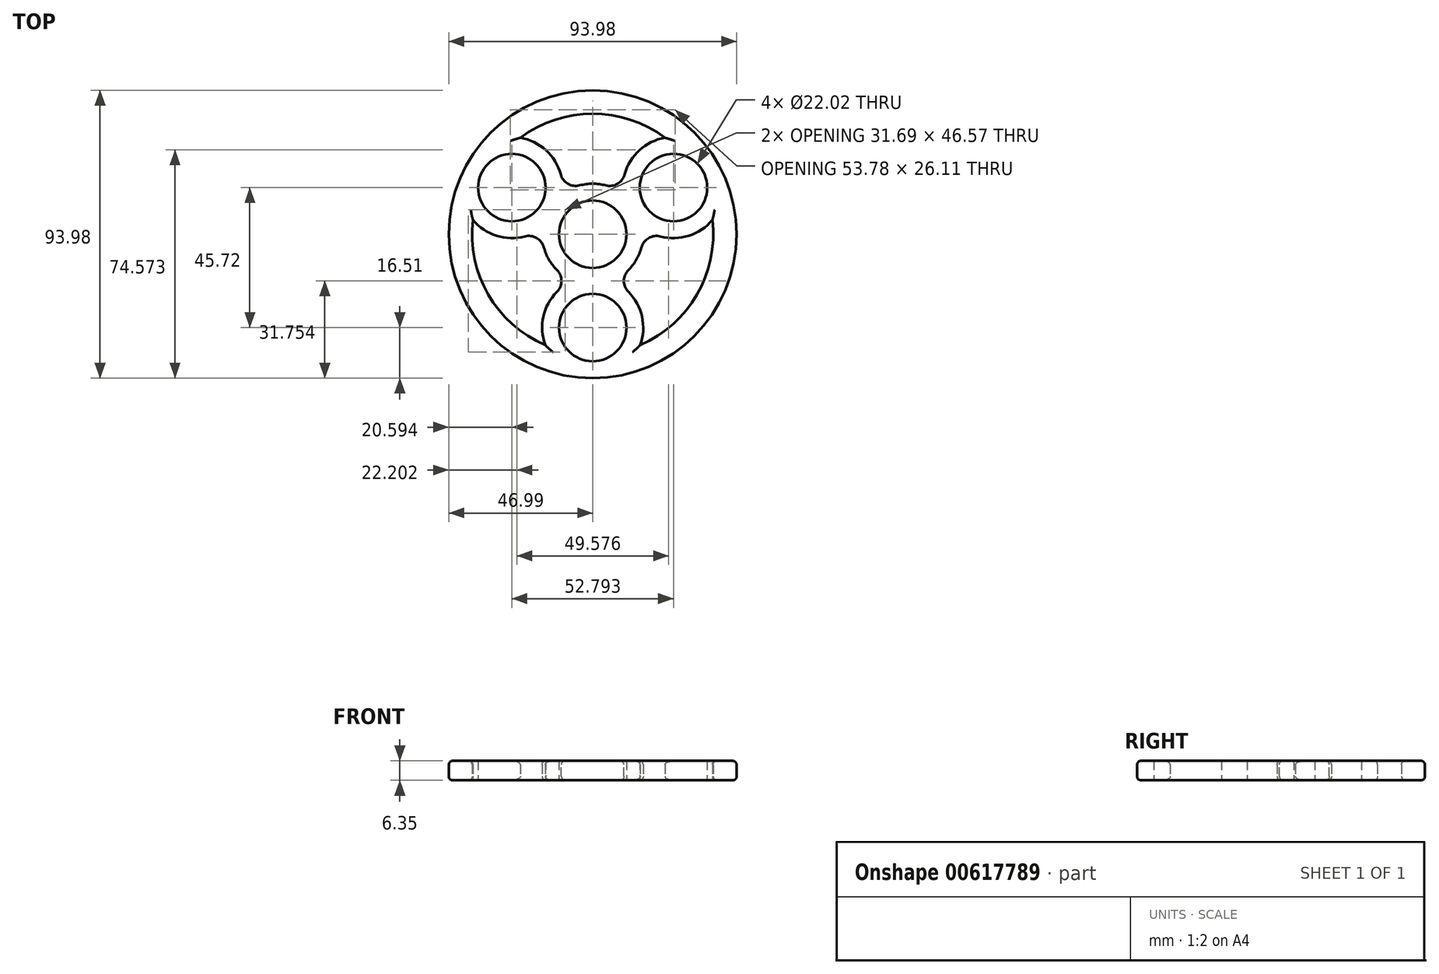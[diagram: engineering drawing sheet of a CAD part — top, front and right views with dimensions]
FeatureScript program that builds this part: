
annotation { "Feature Type Name" : "Feature", "Feature Type Description" : "" }
export const myFeature = defineFeature(function(context is Context, id is Id, definition is map)
    precondition{}
    {
        {
            var Q0;
            Q0=qCreatedBy(makeId("Top.planeOp"),FACE);
            var sketch = newSketch(context, id + "F0", { "sketchPlane" : qUnion([Q0])});
            skCircle(sketch, "E0", {"center": v(0, 0) * mm, "radius": 11.01 * mm});
            skLineSegment(sketch, "E1", {"start": v(0, 0) * mm, "end": v(-26.4, 15.24) * mm});
            skLineSegment(sketch, "E2", {"start": v(0, 0) * mm, "end": v(0, -30.48) * mm});
            skLineSegment(sketch, "E3", {"start": v(0, 0) * mm, "end": v(26.4, 15.24) * mm});
            skCircle(sketch, "E4", {"center": v(-26.4, 15.24) * mm, "radius": 11.01 * mm});
            skCircle(sketch, "E5", {"center": v(26.4, 15.24) * mm, "radius": 11.01 * mm});
            skCircle(sketch, "E6", {"center": v(0, -30.48) * mm, "radius": 11.01 * mm});
            skCircle(sketch, "E7", {"center": v(-26.4, 15.24) * mm, "radius": 16.51 * mm});
            skCircle(sketch, "E8", {"center": v(0, 0) * mm, "radius": 16.51 * mm});
            skCircle(sketch, "E9", {"center": v(0, -30.48) * mm, "radius": 16.51 * mm});
            skCircle(sketch, "E10", {"center": v(26.4, 15.24) * mm, "radius": 16.51 * mm});
            skCircle(sketch, "E11", {"center": v(0, 0) * mm, "radius": 47 * mm});
            skCircle(sketch, "E12", {"center": v(0, 0) * mm, "radius": 39.37 * mm});
            skSolve(sketch);
        }
        {
            var Q0;
            Q0 = qSketchRegion(id + "F0", true);
            var Q1;
            Q1=makeQuery(id+"F0.imprint","IMPRINT",FACE,{"disambiguationData":[TD([[makeQuery(id+"F0.imprint","IMPRINT",EDGE,{"derivedFrom":sQuery(id+"F0.wireOp",EDGE,"E4")}),-1.0]])]});
            var Q2;
            {var subQ1=sQuery(id+"F0.wireOp",EDGE,"E1");var subQ5=sQuery(id+"F0.wireOp",EDGE,"E0");var subQ6=makeQuery(id+"F0.imprint","INTERSECT",VERTEX,{"derivedFrom":[subQ5,subQ1]});Q2=makeQuery(id+"F0.imprint","IMPRINT",FACE,{"disambiguationData":[TD([[makeQuery(id+"F0.imprint","IMPRINT",EDGE,{"disambiguationData":[TD([[subQ6,1.0]])],"derivedFrom":subQ5}),-1.0]])]});}
            var Q3;
            {var subQ0=sQuery(id+"F0.wireOp",EDGE,"E8");var subQ1=sQuery(id+"F0.wireOp",EDGE,"E3");var subQ2=makeQuery(id+"F0.imprint","INTERSECT",VERTEX,{"derivedFrom":[subQ1,subQ0]});Q3=makeQuery(id+"F0.imprint","IMPRINT",FACE,{"disambiguationData":[TD([[makeQuery(id+"F0.imprint","IMPRINT",EDGE,{"disambiguationData":[TD([[subQ2,1.0]])],"derivedFrom":subQ1}),1.0]])]});}
            var Q4;
            {var subQ0=sQuery(id+"F0.wireOp",EDGE,"E8");var subQ1=sQuery(id+"F0.wireOp",EDGE,"E3");var subQ2=makeQuery(id+"F0.imprint","INTERSECT",VERTEX,{"derivedFrom":[subQ1,subQ0]});Q4=makeQuery(id+"F0.imprint","IMPRINT",FACE,{"disambiguationData":[TD([[makeQuery(id+"F0.imprint","IMPRINT",EDGE,{"disambiguationData":[TD([[subQ2,1.0]])],"derivedFrom":subQ1}),-1.0]])]});}
            var Q5;
            Q5=makeQuery(id+"F0.imprint","IMPRINT",FACE,{"disambiguationData":[TD([[makeQuery(id+"F0.imprint","IMPRINT",EDGE,{"derivedFrom":sQuery(id+"F0.wireOp",EDGE,"E5")}),-1.0]])]});
            var Q6;
            {var subQ5=sQuery(id+"F0.wireOp",EDGE,"E3");var subQ6=sQuery(id+"F0.wireOp",EDGE,"E0");var subQ7=makeQuery(id+"F0.imprint","INTERSECT",VERTEX,{"derivedFrom":[subQ6,subQ5]});Q6=makeQuery(id+"F0.imprint","IMPRINT",FACE,{"disambiguationData":[TD([[makeQuery(id+"F0.imprint","IMPRINT",EDGE,{"disambiguationData":[TD([[subQ7,1.0]])],"derivedFrom":subQ6}),-1.0]])]});}
            var Q7;
            {var subQ0=sQuery(id+"F0.wireOp",EDGE,"E8");var subQ1=sQuery(id+"F0.wireOp",EDGE,"E2");var subQ2=makeQuery(id+"F0.imprint","INTERSECT",VERTEX,{"derivedFrom":[subQ1,subQ0]});Q7=makeQuery(id+"F0.imprint","IMPRINT",FACE,{"disambiguationData":[TD([[makeQuery(id+"F0.imprint","IMPRINT",EDGE,{"disambiguationData":[TD([[subQ2,1.0]])],"derivedFrom":subQ1}),1.0]])]});}
            var Q8;
            {var subQ0=sQuery(id+"F0.wireOp",EDGE,"E8");var subQ1=sQuery(id+"F0.wireOp",EDGE,"E2");var subQ2=makeQuery(id+"F0.imprint","INTERSECT",VERTEX,{"derivedFrom":[subQ1,subQ0]});Q8=makeQuery(id+"F0.imprint","IMPRINT",FACE,{"disambiguationData":[TD([[makeQuery(id+"F0.imprint","IMPRINT",EDGE,{"disambiguationData":[TD([[subQ2,1.0]])],"derivedFrom":subQ1}),-1.0]])]});}
            var Q9;
            {var subQ1=sQuery(id+"F0.wireOp",EDGE,"E1");var subQ5=sQuery(id+"F0.wireOp",EDGE,"E0");var subQ6=makeQuery(id+"F0.imprint","INTERSECT",VERTEX,{"derivedFrom":[subQ5,subQ1]});Q9=makeQuery(id+"F0.imprint","IMPRINT",FACE,{"disambiguationData":[TD([[makeQuery(id+"F0.imprint","IMPRINT",EDGE,{"disambiguationData":[TD([[subQ6,-1.0]])],"derivedFrom":subQ5}),-1.0]])]});}
            var Q10;
            {var subQ0=sQuery(id+"F0.wireOp",EDGE,"E8");var subQ1=sQuery(id+"F0.wireOp",EDGE,"E1");var subQ2=makeQuery(id+"F0.imprint","INTERSECT",VERTEX,{"derivedFrom":[subQ1,subQ0]});Q10=makeQuery(id+"F0.imprint","IMPRINT",FACE,{"disambiguationData":[TD([[makeQuery(id+"F0.imprint","IMPRINT",EDGE,{"disambiguationData":[TD([[subQ2,1.0]])],"derivedFrom":subQ1}),-1.0]])]});}
            var Q11;
            {var subQ0=sQuery(id+"F0.wireOp",EDGE,"E8");var subQ1=sQuery(id+"F0.wireOp",EDGE,"E1");var subQ2=makeQuery(id+"F0.imprint","INTERSECT",VERTEX,{"derivedFrom":[subQ1,subQ0]});Q11=makeQuery(id+"F0.imprint","IMPRINT",FACE,{"disambiguationData":[TD([[makeQuery(id+"F0.imprint","IMPRINT",EDGE,{"disambiguationData":[TD([[subQ2,1.0]])],"derivedFrom":subQ1}),1.0]])]});}
            var Q12;
            Q12=makeQuery(id+"F0.imprint","IMPRINT",FACE,{"disambiguationData":[TD([[makeQuery(id+"F0.imprint","IMPRINT",EDGE,{"derivedFrom":sQuery(id+"F0.wireOp",EDGE,"E6")}),-1.0]])]});
            extrude(context, id + "F1", {"entities" : qUnion([Q0, Q1, Q2, Q3, Q4, Q5, Q6, Q7, Q8, Q9, Q10, Q11, Q12]), "depth" : 6.35 * mm, "offsetDistance" : 25.4 * mm});
        }
        {
            var Q0;
            {var subQ0=sQuery(id+"F0.wireOp",EDGE,"E10");var subQ1=sQuery(id+"F0.wireOp",EDGE,"E8");Q0=makeQuery(id+"F1.opExtrude","SWEPT_EDGE",EDGE,{"disambiguationData":[OSD([subQ1,subQ0]),TDD([makeQuery(id+"F0.imprint","INTERSECT",VERTEX,{"disambiguationData":[OD(1.0)],"derivedFrom":[subQ1,subQ0]})])]});}
            var Q1;
            {var subQ0=sQuery(id+"F0.wireOp",EDGE,"E10");var subQ1=sQuery(id+"F0.wireOp",EDGE,"E8");Q1=makeQuery(id+"F1.opExtrude","SWEPT_EDGE",EDGE,{"disambiguationData":[OSD([subQ1,subQ0]),TDD([makeQuery(id+"F0.imprint","INTERSECT",VERTEX,{"disambiguationData":[OD(0.0)],"derivedFrom":[subQ1,subQ0]})])]});}
            var Q2;
            {var subQ0=sQuery(id+"F0.wireOp",EDGE,"E9");var subQ1=sQuery(id+"F0.wireOp",EDGE,"E8");Q2=makeQuery(id+"F1.opExtrude","SWEPT_EDGE",EDGE,{"disambiguationData":[OSD([subQ1,subQ0]),TDD([makeQuery(id+"F0.imprint","INTERSECT",VERTEX,{"disambiguationData":[OD(1.0)],"derivedFrom":[subQ1,subQ0]})])]});}
            var Q3;
            {var subQ0=sQuery(id+"F0.wireOp",EDGE,"E9");var subQ1=sQuery(id+"F0.wireOp",EDGE,"E8");Q3=makeQuery(id+"F1.opExtrude","SWEPT_EDGE",EDGE,{"disambiguationData":[OSD([subQ1,subQ0]),TDD([makeQuery(id+"F0.imprint","INTERSECT",VERTEX,{"disambiguationData":[OD(0.0)],"derivedFrom":[subQ1,subQ0]})])]});}
            var Q4;
            {var subQ0=sQuery(id+"F0.wireOp",EDGE,"E8");var subQ1=sQuery(id+"F0.wireOp",EDGE,"E7");Q4=makeQuery(id+"F1.opExtrude","SWEPT_EDGE",EDGE,{"disambiguationData":[OSD([subQ1,subQ0]),TDD([makeQuery(id+"F0.imprint","INTERSECT",VERTEX,{"disambiguationData":[OD(0.0)],"derivedFrom":[subQ1,subQ0]})])]});}
            var Q5;
            {var subQ0=sQuery(id+"F0.wireOp",EDGE,"E8");var subQ1=sQuery(id+"F0.wireOp",EDGE,"E7");Q5=makeQuery(id+"F1.opExtrude","SWEPT_EDGE",EDGE,{"disambiguationData":[OSD([subQ1,subQ0]),TDD([makeQuery(id+"F0.imprint","INTERSECT",VERTEX,{"disambiguationData":[OD(1.0)],"derivedFrom":[subQ1,subQ0]})])]});}
            fillet(context, id + "F2", {"entities" : qUnion([Q0, Q1, Q2, Q3, Q4, Q5]), "radius" : 5.08 * mm, "tangentPropagation" : true, "allowEdgeOverflow" : false});
        }
        {
            var Q0;
            {var subQ0=sQuery(id+"F0.wireOp",EDGE,"E12");Q0=makeQuery(id+"F1.opExtrude","CAP_EDGE",EDGE,{"disambiguationData":[OSD([subQ0]),TDD([makeQuery(id+"F0.imprint","IMPRINT",EDGE,{"disambiguationData":[TD([[makeQuery(id+"F0.imprint","INTERSECT",VERTEX,{"disambiguationData":[OD(0.0)],"derivedFrom":[sQuery(id+"F0.wireOp",EDGE,"E7"),subQ0]}),1.0]])],"derivedFrom":subQ0})])],"isStart":false});}
            var Q1;
            {var subQ0=sQuery(id+"F0.wireOp",EDGE,"E10");Q1=makeQuery(id+"F1.opExtrude","CAP_EDGE",EDGE,{"disambiguationData":[OSD([subQ0]),TDD([makeQuery(id+"F0.imprint","IMPRINT",EDGE,{"disambiguationData":[TD([[makeQuery(id+"F0.imprint","INTERSECT",VERTEX,{"disambiguationData":[OD(1.0)],"derivedFrom":[sQuery(id+"F0.wireOp",EDGE,"E8"),subQ0]}),1.0]])],"derivedFrom":subQ0})])],"isStart":false});}
            var Q2;
            {var subQ0=sQuery(id+"F0.wireOp",EDGE,"E8");Q2=makeQuery(id+"F1.opExtrude","CAP_EDGE",EDGE,{"disambiguationData":[OSD([subQ0]),TDD([makeQuery(id+"F0.imprint","IMPRINT",EDGE,{"disambiguationData":[TD([[makeQuery(id+"F0.imprint","INTERSECT",VERTEX,{"disambiguationData":[OD(1.0)],"derivedFrom":[sQuery(id+"F0.wireOp",EDGE,"E7"),subQ0]}),1.0]])],"derivedFrom":subQ0})])],"isStart":false});}
            var Q3;
            {var subQ0=sQuery(id+"F0.wireOp",EDGE,"E7");Q3=makeQuery(id+"F1.opExtrude","CAP_EDGE",EDGE,{"disambiguationData":[OSD([subQ0]),TDD([makeQuery(id+"F0.imprint","IMPRINT",EDGE,{"disambiguationData":[TD([[makeQuery(id+"F0.imprint","INTERSECT",VERTEX,{"disambiguationData":[OD(0.0)],"derivedFrom":[subQ0,sQuery(id+"F0.wireOp",EDGE,"E12")]}),1.0]])],"derivedFrom":subQ0})])],"isStart":false});}
            var Q4;
            {var subQ0=sQuery(id+"F0.wireOp",EDGE,"E8");Q4=makeQuery(id+"F1.opExtrude","CAP_EDGE",EDGE,{"disambiguationData":[OSD([subQ0]),TDD([makeQuery(id+"F0.imprint","IMPRINT",EDGE,{"disambiguationData":[TD([[makeQuery(id+"F0.imprint","INTERSECT",VERTEX,{"disambiguationData":[OD(0.0)],"derivedFrom":[subQ0,sQuery(id+"F0.wireOp",EDGE,"E10")]}),1.0]])],"derivedFrom":subQ0})])],"isStart":false});}
            var Q5;
            {var subQ0=sQuery(id+"F0.wireOp",EDGE,"E10");Q5=makeQuery(id+"F1.opExtrude","CAP_EDGE",EDGE,{"disambiguationData":[OSD([subQ0]),TDD([makeQuery(id+"F0.imprint","IMPRINT",EDGE,{"disambiguationData":[TD([[makeQuery(id+"F0.imprint","INTERSECT",VERTEX,{"disambiguationData":[OD(0.0)],"derivedFrom":[sQuery(id+"F0.wireOp",EDGE,"E8"),subQ0]}),-1.0]])],"derivedFrom":subQ0})])],"isStart":false});}
            var Q6;
            {var subQ0=sQuery(id+"F0.wireOp",EDGE,"E9");Q6=makeQuery(id+"F1.opExtrude","CAP_EDGE",EDGE,{"disambiguationData":[OSD([subQ0]),TDD([makeQuery(id+"F0.imprint","IMPRINT",EDGE,{"disambiguationData":[TD([[makeQuery(id+"F0.imprint","INTERSECT",VERTEX,{"disambiguationData":[OD(1.0)],"derivedFrom":[sQuery(id+"F0.wireOp",EDGE,"E8"),subQ0]}),1.0]])],"derivedFrom":subQ0})])],"isStart":false});}
            var Q7;
            {var subQ0=sQuery(id+"F0.wireOp",EDGE,"E12");Q7=makeQuery(id+"F1.opExtrude","CAP_EDGE",EDGE,{"disambiguationData":[OSD([subQ0]),TDD([makeQuery(id+"F0.imprint","IMPRINT",EDGE,{"disambiguationData":[TD([[makeQuery(id+"F0.imprint","INTERSECT",VERTEX,{"disambiguationData":[OD(1.0)],"derivedFrom":[sQuery(id+"F0.wireOp",EDGE,"E9"),subQ0]}),-1.0]])],"derivedFrom":subQ0})])],"isStart":false});}
            var Q8;
            Q8=makeQuery(id+"F1.opExtrude","CAP_EDGE",EDGE,{"disambiguationData":[OSD([sQuery(id+"F0.wireOp",EDGE,"E11")])],"isStart":false});
            var Q9;
            {var subQ0=sQuery(id+"F0.wireOp",EDGE,"E9");Q9=makeQuery(id+"F1.opExtrude","CAP_EDGE",EDGE,{"disambiguationData":[OSD([subQ0]),TDD([makeQuery(id+"F0.imprint","IMPRINT",EDGE,{"disambiguationData":[TD([[makeQuery(id+"F0.imprint","INTERSECT",VERTEX,{"disambiguationData":[OD(0.0)],"derivedFrom":[sQuery(id+"F0.wireOp",EDGE,"E8"),subQ0]}),-1.0]])],"derivedFrom":subQ0})])],"isStart":false});}
            var Q10;
            {var subQ0=sQuery(id+"F0.wireOp",EDGE,"E8");Q10=makeQuery(id+"F1.opExtrude","CAP_EDGE",EDGE,{"disambiguationData":[OSD([subQ0]),TDD([makeQuery(id+"F0.imprint","IMPRINT",EDGE,{"disambiguationData":[TD([[makeQuery(id+"F0.imprint","INTERSECT",VERTEX,{"disambiguationData":[OD(0.0)],"derivedFrom":[sQuery(id+"F0.wireOp",EDGE,"E7"),subQ0]}),-1.0]])],"derivedFrom":subQ0})])],"isStart":false});}
            var Q11;
            {var subQ0=sQuery(id+"F0.wireOp",EDGE,"E7");Q11=makeQuery(id+"F1.opExtrude","CAP_EDGE",EDGE,{"disambiguationData":[OSD([subQ0]),TDD([makeQuery(id+"F0.imprint","IMPRINT",EDGE,{"disambiguationData":[TD([[makeQuery(id+"F0.imprint","INTERSECT",VERTEX,{"disambiguationData":[OD(1.0)],"derivedFrom":[subQ0,sQuery(id+"F0.wireOp",EDGE,"E12")]}),-1.0]])],"derivedFrom":subQ0})])],"isStart":false});}
            var Q12;
            {var subQ0=sQuery(id+"F0.wireOp",EDGE,"E12");Q12=makeQuery(id+"F1.opExtrude","CAP_EDGE",EDGE,{"disambiguationData":[OSD([subQ0]),TDD([makeQuery(id+"F0.imprint","IMPRINT",EDGE,{"disambiguationData":[TD([[makeQuery(id+"F0.imprint","INTERSECT",VERTEX,{"disambiguationData":[OD(1.0)],"derivedFrom":[sQuery(id+"F0.wireOp",EDGE,"E7"),subQ0]}),-1.0]])],"derivedFrom":subQ0})])],"isStart":false});}
            fillet(context, id + "F3", {"entities" : qUnion([Q0, Q1, Q2, Q3, Q4, Q5, Q6, Q7, Q8, Q9, Q10, Q11, Q12]), "radius" : 1.27 * mm, "tangentPropagation" : true, "allowEdgeOverflow" : false});
        }
        {
            var Q0;
            Q0=makeQuery(id+"F1.opExtrude","CAP_EDGE",EDGE,{"disambiguationData":[OSD([sQuery(id+"F0.wireOp",EDGE,"E11")])],"isStart":true});
            var Q1;
            {var subQ0=sQuery(id+"F0.wireOp",EDGE,"E12");Q1=makeQuery(id+"F1.opExtrude","CAP_EDGE",EDGE,{"disambiguationData":[OSD([subQ0]),TDD([makeQuery(id+"F0.imprint","IMPRINT",EDGE,{"disambiguationData":[TD([[makeQuery(id+"F0.imprint","INTERSECT",VERTEX,{"disambiguationData":[OD(0.0)],"derivedFrom":[sQuery(id+"F0.wireOp",EDGE,"E7"),subQ0]}),1.0]])],"derivedFrom":subQ0})])],"isStart":true});}
            var Q2;
            {var subQ0=sQuery(id+"F0.wireOp",EDGE,"E10");Q2=makeQuery(id+"F1.opExtrude","CAP_EDGE",EDGE,{"disambiguationData":[OSD([subQ0]),TDD([makeQuery(id+"F0.imprint","IMPRINT",EDGE,{"disambiguationData":[TD([[makeQuery(id+"F0.imprint","INTERSECT",VERTEX,{"disambiguationData":[OD(1.0)],"derivedFrom":[sQuery(id+"F0.wireOp",EDGE,"E8"),subQ0]}),1.0]])],"derivedFrom":subQ0})])],"isStart":true});}
            var Q3;
            {var subQ0=sQuery(id+"F0.wireOp",EDGE,"E10");Q3=makeQuery(id+"F1.opExtrude","CAP_EDGE",EDGE,{"disambiguationData":[OSD([subQ0]),TDD([makeQuery(id+"F0.imprint","IMPRINT",EDGE,{"disambiguationData":[TD([[makeQuery(id+"F0.imprint","INTERSECT",VERTEX,{"disambiguationData":[OD(0.0)],"derivedFrom":[sQuery(id+"F0.wireOp",EDGE,"E8"),subQ0]}),-1.0]])],"derivedFrom":subQ0})])],"isStart":true});}
            var Q4;
            {var subQ0=sQuery(id+"F0.wireOp",EDGE,"E8");Q4=makeQuery(id+"F1.opExtrude","CAP_EDGE",EDGE,{"disambiguationData":[OSD([subQ0]),TDD([makeQuery(id+"F0.imprint","IMPRINT",EDGE,{"disambiguationData":[TD([[makeQuery(id+"F0.imprint","INTERSECT",VERTEX,{"disambiguationData":[OD(0.0)],"derivedFrom":[subQ0,sQuery(id+"F0.wireOp",EDGE,"E10")]}),1.0]])],"derivedFrom":subQ0})])],"isStart":true});}
            var Q5;
            {var subQ0=sQuery(id+"F0.wireOp",EDGE,"E8");Q5=makeQuery(id+"F1.opExtrude","CAP_EDGE",EDGE,{"disambiguationData":[OSD([subQ0]),TDD([makeQuery(id+"F0.imprint","IMPRINT",EDGE,{"disambiguationData":[TD([[makeQuery(id+"F0.imprint","INTERSECT",VERTEX,{"disambiguationData":[OD(1.0)],"derivedFrom":[sQuery(id+"F0.wireOp",EDGE,"E7"),subQ0]}),1.0]])],"derivedFrom":subQ0})])],"isStart":true});}
            var Q6;
            {var subQ0=sQuery(id+"F0.wireOp",EDGE,"E7");Q6=makeQuery(id+"F1.opExtrude","CAP_EDGE",EDGE,{"disambiguationData":[OSD([subQ0]),TDD([makeQuery(id+"F0.imprint","IMPRINT",EDGE,{"disambiguationData":[TD([[makeQuery(id+"F0.imprint","INTERSECT",VERTEX,{"disambiguationData":[OD(0.0)],"derivedFrom":[subQ0,sQuery(id+"F0.wireOp",EDGE,"E12")]}),1.0]])],"derivedFrom":subQ0})])],"isStart":true});}
            var Q7;
            {var subQ0=sQuery(id+"F0.wireOp",EDGE,"E7");Q7=makeQuery(id+"F1.opExtrude","CAP_EDGE",EDGE,{"disambiguationData":[OSD([subQ0]),TDD([makeQuery(id+"F0.imprint","IMPRINT",EDGE,{"disambiguationData":[TD([[makeQuery(id+"F0.imprint","INTERSECT",VERTEX,{"disambiguationData":[OD(1.0)],"derivedFrom":[subQ0,sQuery(id+"F0.wireOp",EDGE,"E12")]}),-1.0]])],"derivedFrom":subQ0})])],"isStart":true});}
            var Q8;
            {var subQ0=sQuery(id+"F0.wireOp",EDGE,"E8");Q8=makeQuery(id+"F1.opExtrude","CAP_EDGE",EDGE,{"disambiguationData":[OSD([subQ0]),TDD([makeQuery(id+"F0.imprint","IMPRINT",EDGE,{"disambiguationData":[TD([[makeQuery(id+"F0.imprint","INTERSECT",VERTEX,{"disambiguationData":[OD(0.0)],"derivedFrom":[sQuery(id+"F0.wireOp",EDGE,"E7"),subQ0]}),-1.0]])],"derivedFrom":subQ0})])],"isStart":true});}
            var Q9;
            {var subQ0=sQuery(id+"F0.wireOp",EDGE,"E9");Q9=makeQuery(id+"F1.opExtrude","CAP_EDGE",EDGE,{"disambiguationData":[OSD([subQ0]),TDD([makeQuery(id+"F0.imprint","IMPRINT",EDGE,{"disambiguationData":[TD([[makeQuery(id+"F0.imprint","INTERSECT",VERTEX,{"disambiguationData":[OD(0.0)],"derivedFrom":[sQuery(id+"F0.wireOp",EDGE,"E8"),subQ0]}),-1.0]])],"derivedFrom":subQ0})])],"isStart":true});}
            var Q10;
            {var subQ0=sQuery(id+"F0.wireOp",EDGE,"E12");Q10=makeQuery(id+"F1.opExtrude","CAP_EDGE",EDGE,{"disambiguationData":[OSD([subQ0]),TDD([makeQuery(id+"F0.imprint","IMPRINT",EDGE,{"disambiguationData":[TD([[makeQuery(id+"F0.imprint","INTERSECT",VERTEX,{"disambiguationData":[OD(1.0)],"derivedFrom":[sQuery(id+"F0.wireOp",EDGE,"E7"),subQ0]}),-1.0]])],"derivedFrom":subQ0})])],"isStart":true});}
            var Q11;
            {var subQ0=sQuery(id+"F0.wireOp",EDGE,"E12");Q11=makeQuery(id+"F1.opExtrude","CAP_EDGE",EDGE,{"disambiguationData":[OSD([subQ0]),TDD([makeQuery(id+"F0.imprint","IMPRINT",EDGE,{"disambiguationData":[TD([[makeQuery(id+"F0.imprint","INTERSECT",VERTEX,{"disambiguationData":[OD(1.0)],"derivedFrom":[sQuery(id+"F0.wireOp",EDGE,"E9"),subQ0]}),-1.0]])],"derivedFrom":subQ0})])],"isStart":true});}
            var Q12;
            {var subQ0=sQuery(id+"F0.wireOp",EDGE,"E9");Q12=makeQuery(id+"F1.opExtrude","CAP_EDGE",EDGE,{"disambiguationData":[OSD([subQ0]),TDD([makeQuery(id+"F0.imprint","IMPRINT",EDGE,{"disambiguationData":[TD([[makeQuery(id+"F0.imprint","INTERSECT",VERTEX,{"disambiguationData":[OD(1.0)],"derivedFrom":[sQuery(id+"F0.wireOp",EDGE,"E8"),subQ0]}),1.0]])],"derivedFrom":subQ0})])],"isStart":true});}
            fillet(context, id + "F4", {"entities" : qUnion([Q0, Q1, Q2, Q3, Q4, Q5, Q6, Q7, Q8, Q9, Q10, Q11, Q12]), "radius" : 1.27 * mm, "tangentPropagation" : true, "allowEdgeOverflow" : false});
        }
    });
